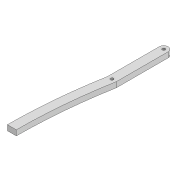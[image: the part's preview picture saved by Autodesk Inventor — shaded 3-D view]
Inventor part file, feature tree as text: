
AUTODESK INVENTOR PART (.ipt)
format: ipt  version: 2022 (Build 260153000, 153)  size: 112,640 bytes
history: native  units: mm
features: extrude x2, sketch x2
ambient origin geometry x8: Origin, YZ Plane, XZ Plane, XY Plane, X Axis, Y Axis, Z Axis, Center Point
bodies: Solid1 (feature_tree)
feature tree (4):
  extrude  "Extrusion1"  Depth=3.3mm
  extrude  "Extrusion2"  Depth=312.648mm
  sketch  "Sketch1"  dims[d0=3.3mm d1=3.3mm]
  sketch  "Sketch2"  dims[d2=10.0mm d3=312.648mm d6=6.0mm d7=0.0mm d10=3.3mm d11=42.6mm d12=3.3mm d13=254.274mm d16=600.0mm d17=600.0mm d18=10.0mm d19=0.0mm]
